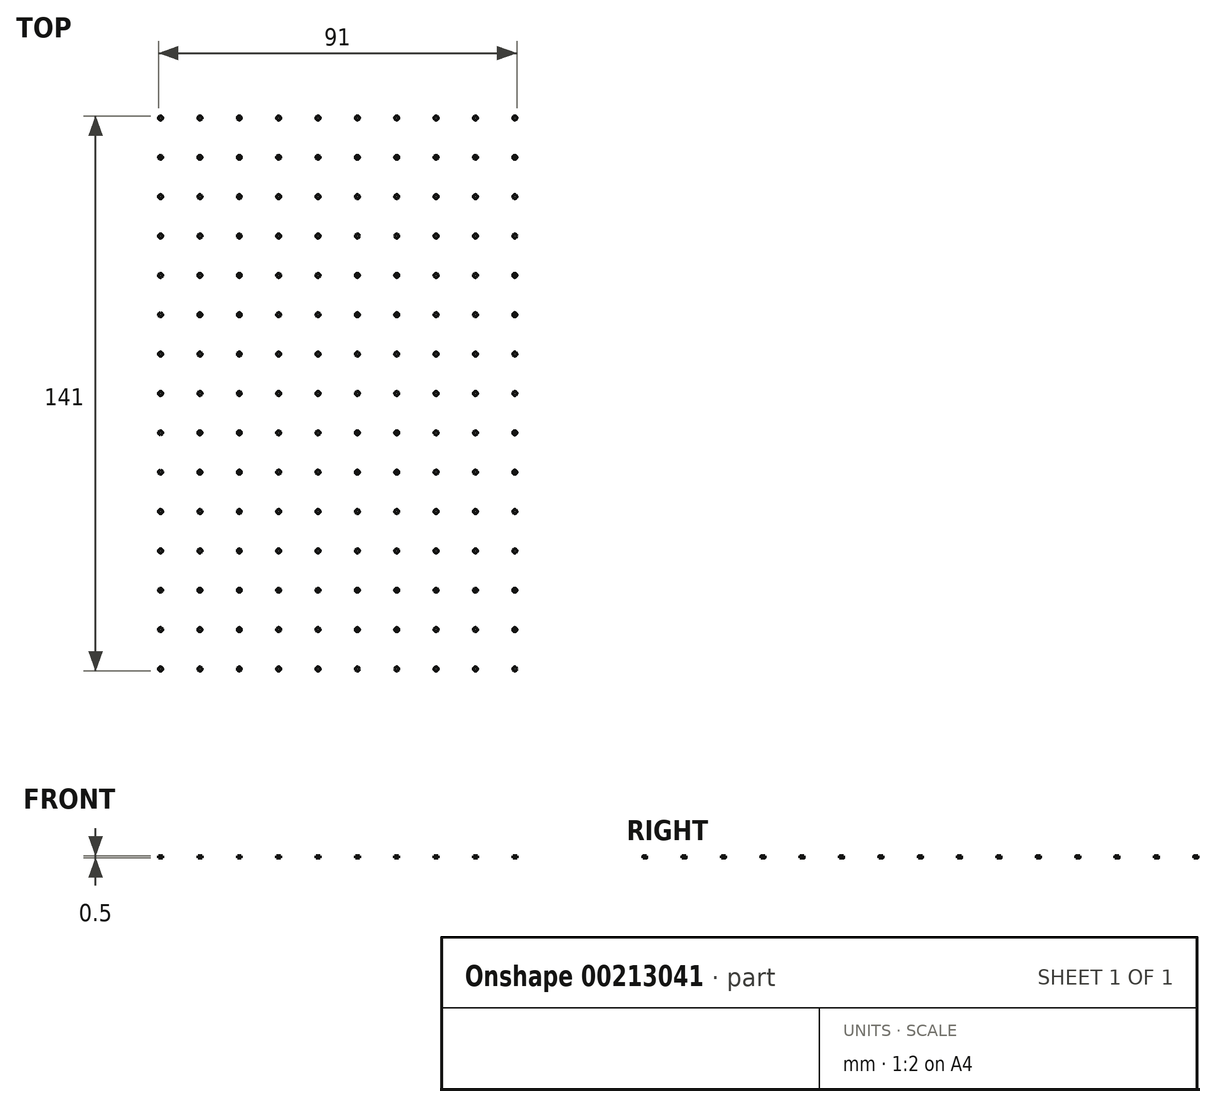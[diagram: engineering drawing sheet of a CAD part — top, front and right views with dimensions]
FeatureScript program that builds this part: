
annotation { "Feature Type Name" : "Feature", "Feature Type Description" : "" }
export const myFeature = defineFeature(function(context is Context, id is Id, definition is map)
    precondition{}
    {
        {
            var Q0;
            Q0=qCreatedBy(makeId("Top.planeOp"),FACE);
            var sketch = newSketch(context, id + "F0", { "sketchPlane" : qUnion([Q0])});
            skCircle(sketch, "E0", {"center": v(-61.45, -31.33) * mm, "radius": 0.5 * mm});
            skCircle(sketch, "E1.0.1.0", {"center": v(-61.45, -21.33) * mm, "radius": 0.5 * mm});
            skCircle(sketch, "E1.0.2.0", {"center": v(-61.45, -11.33) * mm, "radius": 0.5 * mm});
            skCircle(sketch, "E1.1.0.0", {"center": v(-51.45, -31.33) * mm, "radius": 0.5 * mm});
            skCircle(sketch, "E1.1.1.0", {"center": v(-51.45, -21.33) * mm, "radius": 0.5 * mm});
            skCircle(sketch, "E1.1.2.0", {"center": v(-51.45, -11.33) * mm, "radius": 0.5 * mm});
            skCircle(sketch, "E1.2.0.0", {"center": v(-41.45, -31.33) * mm, "radius": 0.5 * mm});
            skCircle(sketch, "E1.2.1.0", {"center": v(-41.45, -21.33) * mm, "radius": 0.5 * mm});
            skCircle(sketch, "E1.2.2.0", {"center": v(-41.45, -11.33) * mm, "radius": 0.5 * mm});
            skCircle(sketch, "E1.3.0.0", {"center": v(-31.45, -31.33) * mm, "radius": 0.5 * mm});
            skCircle(sketch, "E1.3.1.0", {"center": v(-31.45, -21.33) * mm, "radius": 0.5 * mm});
            skCircle(sketch, "E1.3.2.0", {"center": v(-31.45, -11.33) * mm, "radius": 0.5 * mm});
            skLineSegment(sketch, "E1.direction1", {"start": v(-61.45, -31.33) * mm, "end": v(-51.45, -31.33) * mm, "construction": true});
            skLineSegment(sketch, "E1.direction2", {"start": v(-61.45, -31.33) * mm, "end": v(-61.45, -21.33) * mm, "construction": true});
            skCircle(sketch, "E2.0.0.3", {"center": v(-61.45, -1.33) * mm, "radius": 0.5 * mm});
            skCircle(sketch, "E2.0.0.4", {"center": v(-61.45, 8.67) * mm, "radius": 0.5 * mm});
            skCircle(sketch, "E2.0.0.5", {"center": v(-61.45, 18.67) * mm, "radius": 0.5 * mm});
            skCircle(sketch, "E2.0.0.6", {"center": v(-61.45, 28.67) * mm, "radius": 0.5 * mm});
            skCircle(sketch, "E2.0.0.7", {"center": v(-61.45, 38.67) * mm, "radius": 0.5 * mm});
            skCircle(sketch, "E2.0.0.8", {"center": v(-61.45, 48.67) * mm, "radius": 0.5 * mm});
            skCircle(sketch, "E2.0.0.9", {"center": v(-61.45, 58.67) * mm, "radius": 0.5 * mm});
            skCircle(sketch, "E2.0.0.10", {"center": v(-61.45, 68.67) * mm, "radius": 0.5 * mm});
            skCircle(sketch, "E2.0.0.11", {"center": v(-61.45, 78.67) * mm, "radius": 0.5 * mm});
            skCircle(sketch, "E2.0.0.12", {"center": v(-61.45, 88.67) * mm, "radius": 0.5 * mm});
            skCircle(sketch, "E2.0.0.13", {"center": v(-61.45, 98.67) * mm, "radius": 0.5 * mm});
            skCircle(sketch, "E2.0.0.14", {"center": v(-61.45, 108.67) * mm, "radius": 0.5 * mm});
            skCircle(sketch, "E2.0.1.3", {"center": v(-51.45, -1.33) * mm, "radius": 0.5 * mm});
            skCircle(sketch, "E2.0.1.4", {"center": v(-51.45, 8.67) * mm, "radius": 0.5 * mm});
            skCircle(sketch, "E2.0.1.5", {"center": v(-51.45, 18.67) * mm, "radius": 0.5 * mm});
            skCircle(sketch, "E2.0.1.6", {"center": v(-51.45, 28.67) * mm, "radius": 0.5 * mm});
            skCircle(sketch, "E2.0.1.7", {"center": v(-51.45, 38.67) * mm, "radius": 0.5 * mm});
            skCircle(sketch, "E2.0.1.8", {"center": v(-51.45, 48.67) * mm, "radius": 0.5 * mm});
            skCircle(sketch, "E2.0.1.9", {"center": v(-51.45, 58.67) * mm, "radius": 0.5 * mm});
            skCircle(sketch, "E2.0.1.10", {"center": v(-51.45, 68.67) * mm, "radius": 0.5 * mm});
            skCircle(sketch, "E2.0.1.11", {"center": v(-51.45, 78.67) * mm, "radius": 0.5 * mm});
            skCircle(sketch, "E2.0.1.12", {"center": v(-51.45, 88.67) * mm, "radius": 0.5 * mm});
            skCircle(sketch, "E2.0.1.13", {"center": v(-51.45, 98.67) * mm, "radius": 0.5 * mm});
            skCircle(sketch, "E2.0.1.14", {"center": v(-51.45, 108.67) * mm, "radius": 0.5 * mm});
            skCircle(sketch, "E2.0.2.3", {"center": v(-41.45, -1.33) * mm, "radius": 0.5 * mm});
            skCircle(sketch, "E2.0.2.4", {"center": v(-41.45, 8.67) * mm, "radius": 0.5 * mm});
            skCircle(sketch, "E2.0.2.5", {"center": v(-41.45, 18.67) * mm, "radius": 0.5 * mm});
            skCircle(sketch, "E2.0.2.6", {"center": v(-41.45, 28.67) * mm, "radius": 0.5 * mm});
            skCircle(sketch, "E2.0.2.7", {"center": v(-41.45, 38.67) * mm, "radius": 0.5 * mm});
            skCircle(sketch, "E2.0.2.8", {"center": v(-41.45, 48.67) * mm, "radius": 0.5 * mm});
            skCircle(sketch, "E2.0.2.9", {"center": v(-41.45, 58.67) * mm, "radius": 0.5 * mm});
            skCircle(sketch, "E2.0.2.10", {"center": v(-41.45, 68.67) * mm, "radius": 0.5 * mm});
            skCircle(sketch, "E2.0.2.11", {"center": v(-41.45, 78.67) * mm, "radius": 0.5 * mm});
            skCircle(sketch, "E2.0.2.12", {"center": v(-41.45, 88.67) * mm, "radius": 0.5 * mm});
            skCircle(sketch, "E2.0.2.13", {"center": v(-41.45, 98.67) * mm, "radius": 0.5 * mm});
            skCircle(sketch, "E2.0.2.14", {"center": v(-41.45, 108.67) * mm, "radius": 0.5 * mm});
            skCircle(sketch, "E2.0.3.3", {"center": v(-31.45, -1.33) * mm, "radius": 0.5 * mm});
            skCircle(sketch, "E2.0.3.4", {"center": v(-31.45, 8.67) * mm, "radius": 0.5 * mm});
            skCircle(sketch, "E2.0.3.5", {"center": v(-31.45, 18.67) * mm, "radius": 0.5 * mm});
            skCircle(sketch, "E2.0.3.6", {"center": v(-31.45, 28.67) * mm, "radius": 0.5 * mm});
            skCircle(sketch, "E2.0.3.7", {"center": v(-31.45, 38.67) * mm, "radius": 0.5 * mm});
            skCircle(sketch, "E2.0.3.8", {"center": v(-31.45, 48.67) * mm, "radius": 0.5 * mm});
            skCircle(sketch, "E2.0.3.9", {"center": v(-31.45, 58.67) * mm, "radius": 0.5 * mm});
            skCircle(sketch, "E2.0.3.10", {"center": v(-31.45, 68.67) * mm, "radius": 0.5 * mm});
            skCircle(sketch, "E2.0.3.11", {"center": v(-31.45, 78.67) * mm, "radius": 0.5 * mm});
            skCircle(sketch, "E2.0.3.12", {"center": v(-31.45, 88.67) * mm, "radius": 0.5 * mm});
            skCircle(sketch, "E2.0.3.13", {"center": v(-31.45, 98.67) * mm, "radius": 0.5 * mm});
            skCircle(sketch, "E2.0.3.14", {"center": v(-31.45, 108.67) * mm, "radius": 0.5 * mm});
            skCircle(sketch, "E3.0.4.0", {"center": v(-21.45, -31.33) * mm, "radius": 0.5 * mm});
            skCircle(sketch, "E3.0.4.1", {"center": v(-21.45, -21.33) * mm, "radius": 0.5 * mm});
            skCircle(sketch, "E3.0.4.2", {"center": v(-21.45, -11.33) * mm, "radius": 0.5 * mm});
            skCircle(sketch, "E3.0.4.3", {"center": v(-21.45, -1.33) * mm, "radius": 0.5 * mm});
            skCircle(sketch, "E3.0.4.4", {"center": v(-21.45, 8.67) * mm, "radius": 0.5 * mm});
            skCircle(sketch, "E3.0.4.5", {"center": v(-21.45, 18.67) * mm, "radius": 0.5 * mm});
            skCircle(sketch, "E3.0.4.6", {"center": v(-21.45, 28.67) * mm, "radius": 0.5 * mm});
            skCircle(sketch, "E3.0.4.7", {"center": v(-21.45, 38.67) * mm, "radius": 0.5 * mm});
            skCircle(sketch, "E3.0.4.8", {"center": v(-21.45, 48.67) * mm, "radius": 0.5 * mm});
            skCircle(sketch, "E3.0.4.9", {"center": v(-21.45, 58.67) * mm, "radius": 0.5 * mm});
            skCircle(sketch, "E3.0.4.10", {"center": v(-21.45, 68.67) * mm, "radius": 0.5 * mm});
            skCircle(sketch, "E3.0.4.11", {"center": v(-21.45, 78.67) * mm, "radius": 0.5 * mm});
            skCircle(sketch, "E3.0.4.12", {"center": v(-21.45, 88.67) * mm, "radius": 0.5 * mm});
            skCircle(sketch, "E3.0.4.13", {"center": v(-21.45, 98.67) * mm, "radius": 0.5 * mm});
            skCircle(sketch, "E3.0.4.14", {"center": v(-21.45, 108.67) * mm, "radius": 0.5 * mm});
            skCircle(sketch, "E3.0.5.0", {"center": v(-11.45, -31.33) * mm, "radius": 0.5 * mm});
            skCircle(sketch, "E3.0.5.1", {"center": v(-11.45, -21.33) * mm, "radius": 0.5 * mm});
            skCircle(sketch, "E3.0.5.2", {"center": v(-11.45, -11.33) * mm, "radius": 0.5 * mm});
            skCircle(sketch, "E3.0.5.3", {"center": v(-11.45, -1.33) * mm, "radius": 0.5 * mm});
            skCircle(sketch, "E3.0.5.4", {"center": v(-11.45, 8.67) * mm, "radius": 0.5 * mm});
            skCircle(sketch, "E3.0.5.5", {"center": v(-11.45, 18.67) * mm, "radius": 0.5 * mm});
            skCircle(sketch, "E3.0.5.6", {"center": v(-11.45, 28.67) * mm, "radius": 0.5 * mm});
            skCircle(sketch, "E3.0.5.7", {"center": v(-11.45, 38.67) * mm, "radius": 0.5 * mm});
            skCircle(sketch, "E3.0.5.8", {"center": v(-11.45, 48.67) * mm, "radius": 0.5 * mm});
            skCircle(sketch, "E3.0.5.9", {"center": v(-11.45, 58.67) * mm, "radius": 0.5 * mm});
            skCircle(sketch, "E3.0.5.10", {"center": v(-11.45, 68.67) * mm, "radius": 0.5 * mm});
            skCircle(sketch, "E3.0.5.11", {"center": v(-11.45, 78.67) * mm, "radius": 0.5 * mm});
            skCircle(sketch, "E3.0.5.12", {"center": v(-11.45, 88.67) * mm, "radius": 0.5 * mm});
            skCircle(sketch, "E3.0.5.13", {"center": v(-11.45, 98.67) * mm, "radius": 0.5 * mm});
            skCircle(sketch, "E3.0.5.14", {"center": v(-11.45, 108.67) * mm, "radius": 0.5 * mm});
            skCircle(sketch, "E3.0.6.0", {"center": v(-1.45, -31.33) * mm, "radius": 0.5 * mm});
            skCircle(sketch, "E3.0.6.1", {"center": v(-1.45, -21.33) * mm, "radius": 0.5 * mm});
            skCircle(sketch, "E3.0.6.2", {"center": v(-1.45, -11.33) * mm, "radius": 0.5 * mm});
            skCircle(sketch, "E3.0.6.3", {"center": v(-1.45, -1.33) * mm, "radius": 0.5 * mm});
            skCircle(sketch, "E3.0.6.4", {"center": v(-1.45, 8.67) * mm, "radius": 0.5 * mm});
            skCircle(sketch, "E3.0.6.5", {"center": v(-1.45, 18.67) * mm, "radius": 0.5 * mm});
            skCircle(sketch, "E3.0.6.6", {"center": v(-1.45, 28.67) * mm, "radius": 0.5 * mm});
            skCircle(sketch, "E3.0.6.7", {"center": v(-1.45, 38.67) * mm, "radius": 0.5 * mm});
            skCircle(sketch, "E3.0.6.8", {"center": v(-1.45, 48.67) * mm, "radius": 0.5 * mm});
            skCircle(sketch, "E3.0.6.9", {"center": v(-1.45, 58.67) * mm, "radius": 0.5 * mm});
            skCircle(sketch, "E3.0.6.10", {"center": v(-1.45, 68.67) * mm, "radius": 0.5 * mm});
            skCircle(sketch, "E3.0.6.11", {"center": v(-1.45, 78.67) * mm, "radius": 0.5 * mm});
            skCircle(sketch, "E3.0.6.12", {"center": v(-1.45, 88.67) * mm, "radius": 0.5 * mm});
            skCircle(sketch, "E3.0.6.13", {"center": v(-1.45, 98.67) * mm, "radius": 0.5 * mm});
            skCircle(sketch, "E3.0.6.14", {"center": v(-1.45, 108.67) * mm, "radius": 0.5 * mm});
            skCircle(sketch, "E3.0.7.0", {"center": v(8.55, -31.33) * mm, "radius": 0.5 * mm});
            skCircle(sketch, "E3.0.7.1", {"center": v(8.55, -21.33) * mm, "radius": 0.5 * mm});
            skCircle(sketch, "E3.0.7.2", {"center": v(8.55, -11.33) * mm, "radius": 0.5 * mm});
            skCircle(sketch, "E3.0.7.3", {"center": v(8.55, -1.33) * mm, "radius": 0.5 * mm});
            skCircle(sketch, "E3.0.7.4", {"center": v(8.55, 8.67) * mm, "radius": 0.5 * mm});
            skCircle(sketch, "E3.0.7.5", {"center": v(8.55, 18.67) * mm, "radius": 0.5 * mm});
            skCircle(sketch, "E3.0.7.6", {"center": v(8.55, 28.67) * mm, "radius": 0.5 * mm});
            skCircle(sketch, "E3.0.7.7", {"center": v(8.55, 38.67) * mm, "radius": 0.5 * mm});
            skCircle(sketch, "E3.0.7.8", {"center": v(8.55, 48.67) * mm, "radius": 0.5 * mm});
            skCircle(sketch, "E3.0.7.9", {"center": v(8.55, 58.67) * mm, "radius": 0.5 * mm});
            skCircle(sketch, "E3.0.7.10", {"center": v(8.55, 68.67) * mm, "radius": 0.5 * mm});
            skCircle(sketch, "E3.0.7.11", {"center": v(8.55, 78.67) * mm, "radius": 0.5 * mm});
            skCircle(sketch, "E3.0.7.12", {"center": v(8.55, 88.67) * mm, "radius": 0.5 * mm});
            skCircle(sketch, "E3.0.7.13", {"center": v(8.55, 98.67) * mm, "radius": 0.5 * mm});
            skCircle(sketch, "E3.0.7.14", {"center": v(8.55, 108.67) * mm, "radius": 0.5 * mm});
            skCircle(sketch, "E3.0.8.0", {"center": v(18.55, -31.33) * mm, "radius": 0.5 * mm});
            skCircle(sketch, "E3.0.8.1", {"center": v(18.55, -21.33) * mm, "radius": 0.5 * mm});
            skCircle(sketch, "E3.0.8.2", {"center": v(18.55, -11.33) * mm, "radius": 0.5 * mm});
            skCircle(sketch, "E3.0.8.3", {"center": v(18.55, -1.33) * mm, "radius": 0.5 * mm});
            skCircle(sketch, "E3.0.8.4", {"center": v(18.55, 8.67) * mm, "radius": 0.5 * mm});
            skCircle(sketch, "E3.0.8.5", {"center": v(18.55, 18.67) * mm, "radius": 0.5 * mm});
            skCircle(sketch, "E3.0.8.6", {"center": v(18.55, 28.67) * mm, "radius": 0.5 * mm});
            skCircle(sketch, "E3.0.8.7", {"center": v(18.55, 38.67) * mm, "radius": 0.5 * mm});
            skCircle(sketch, "E3.0.8.8", {"center": v(18.55, 48.67) * mm, "radius": 0.5 * mm});
            skCircle(sketch, "E3.0.8.9", {"center": v(18.55, 58.67) * mm, "radius": 0.5 * mm});
            skCircle(sketch, "E3.0.8.10", {"center": v(18.55, 68.67) * mm, "radius": 0.5 * mm});
            skCircle(sketch, "E3.0.8.11", {"center": v(18.55, 78.67) * mm, "radius": 0.5 * mm});
            skCircle(sketch, "E3.0.8.12", {"center": v(18.55, 88.67) * mm, "radius": 0.5 * mm});
            skCircle(sketch, "E3.0.8.13", {"center": v(18.55, 98.67) * mm, "radius": 0.5 * mm});
            skCircle(sketch, "E3.0.8.14", {"center": v(18.55, 108.67) * mm, "radius": 0.5 * mm});
            skCircle(sketch, "E3.0.9.0", {"center": v(28.55, -31.33) * mm, "radius": 0.5 * mm});
            skCircle(sketch, "E3.0.9.1", {"center": v(28.55, -21.33) * mm, "radius": 0.5 * mm});
            skCircle(sketch, "E3.0.9.2", {"center": v(28.55, -11.33) * mm, "radius": 0.5 * mm});
            skCircle(sketch, "E3.0.9.3", {"center": v(28.55, -1.33) * mm, "radius": 0.5 * mm});
            skCircle(sketch, "E3.0.9.4", {"center": v(28.55, 8.67) * mm, "radius": 0.5 * mm});
            skCircle(sketch, "E3.0.9.5", {"center": v(28.55, 18.67) * mm, "radius": 0.5 * mm});
            skCircle(sketch, "E3.0.9.6", {"center": v(28.55, 28.67) * mm, "radius": 0.5 * mm});
            skCircle(sketch, "E3.0.9.7", {"center": v(28.55, 38.67) * mm, "radius": 0.5 * mm});
            skCircle(sketch, "E3.0.9.8", {"center": v(28.55, 48.67) * mm, "radius": 0.5 * mm});
            skCircle(sketch, "E3.0.9.9", {"center": v(28.55, 58.67) * mm, "radius": 0.5 * mm});
            skCircle(sketch, "E3.0.9.10", {"center": v(28.55, 68.67) * mm, "radius": 0.5 * mm});
            skCircle(sketch, "E3.0.9.11", {"center": v(28.55, 78.67) * mm, "radius": 0.5 * mm});
            skCircle(sketch, "E3.0.9.12", {"center": v(28.55, 88.67) * mm, "radius": 0.5 * mm});
            skCircle(sketch, "E3.0.9.13", {"center": v(28.55, 98.67) * mm, "radius": 0.5 * mm});
            skCircle(sketch, "E3.0.9.14", {"center": v(28.55, 108.67) * mm, "radius": 0.5 * mm});
            skSolve(sketch);
        }
        {
            var Q0;
            Q0=makeQuery(id+"F0.imprint","IMPRINT",FACE,{"disambiguationData":[TD([[makeQuery(id+"F0.imprint","IMPRINT",EDGE,{"derivedFrom":sQuery(id+"F0.wireOp",EDGE,"E1.0.2.0")}),1.0]])]});
            var Q1;
            Q1=makeQuery(id+"F0.imprint","IMPRINT",FACE,{"disambiguationData":[TD([[makeQuery(id+"F0.imprint","IMPRINT",EDGE,{"derivedFrom":sQuery(id+"F0.wireOp",EDGE,"E1.3.2.0")}),1.0]])]});
            var Q2;
            Q2=makeQuery(id+"F0.imprint","IMPRINT",FACE,{"disambiguationData":[TD([[makeQuery(id+"F0.imprint","IMPRINT",EDGE,{"derivedFrom":sQuery(id+"F0.wireOp",EDGE,"E1.3.1.0")}),1.0]])]});
            var Q3;
            Q3=makeQuery(id+"F0.imprint","IMPRINT",FACE,{"disambiguationData":[TD([[makeQuery(id+"F0.imprint","IMPRINT",EDGE,{"derivedFrom":sQuery(id+"F0.wireOp",EDGE,"E1.3.0.0")}),1.0]])]});
            var Q4;
            Q4=makeQuery(id+"F0.imprint","IMPRINT",FACE,{"disambiguationData":[TD([[makeQuery(id+"F0.imprint","IMPRINT",EDGE,{"derivedFrom":sQuery(id+"F0.wireOp",EDGE,"E1.2.2.0")}),1.0]])]});
            var Q5;
            Q5=makeQuery(id+"F0.imprint","IMPRINT",FACE,{"disambiguationData":[TD([[makeQuery(id+"F0.imprint","IMPRINT",EDGE,{"derivedFrom":sQuery(id+"F0.wireOp",EDGE,"E1.2.1.0")}),1.0]])]});
            var Q6;
            Q6=makeQuery(id+"F0.imprint","IMPRINT",FACE,{"disambiguationData":[TD([[makeQuery(id+"F0.imprint","IMPRINT",EDGE,{"derivedFrom":sQuery(id+"F0.wireOp",EDGE,"E1.2.0.0")}),1.0]])]});
            var Q7;
            Q7=makeQuery(id+"F0.imprint","IMPRINT",FACE,{"disambiguationData":[TD([[makeQuery(id+"F0.imprint","IMPRINT",EDGE,{"derivedFrom":sQuery(id+"F0.wireOp",EDGE,"E1.1.2.0")}),1.0]])]});
            var Q8;
            Q8=makeQuery(id+"F0.imprint","IMPRINT",FACE,{"disambiguationData":[TD([[makeQuery(id+"F0.imprint","IMPRINT",EDGE,{"derivedFrom":sQuery(id+"F0.wireOp",EDGE,"E1.1.1.0")}),1.0]])]});
            var Q9;
            Q9=makeQuery(id+"F0.imprint","IMPRINT",FACE,{"disambiguationData":[TD([[makeQuery(id+"F0.imprint","IMPRINT",EDGE,{"derivedFrom":sQuery(id+"F0.wireOp",EDGE,"E1.1.0.0")}),1.0]])]});
            var Q10;
            Q10=makeQuery(id+"F0.imprint","IMPRINT",FACE,{"disambiguationData":[TD([[makeQuery(id+"F0.imprint","IMPRINT",EDGE,{"derivedFrom":sQuery(id+"F0.wireOp",EDGE,"E1.0.1.0")}),1.0]])]});
            var Q11;
            Q11=makeQuery(id+"F0.imprint","IMPRINT",FACE,{"disambiguationData":[TD([[makeQuery(id+"F0.imprint","IMPRINT",EDGE,{"derivedFrom":sQuery(id+"F0.wireOp",EDGE,"E0")}),1.0]])]});
            var Q12;
            Q12=makeQuery(id+"F0.imprint","IMPRINT",FACE,{"disambiguationData":[TD([[makeQuery(id+"F0.imprint","IMPRINT",EDGE,{"derivedFrom":sQuery(id+"F0.wireOp",EDGE,"E2.0.2.13")}),1.0]])]});
            var Q13;
            Q13=makeQuery(id+"F0.imprint","IMPRINT",FACE,{"disambiguationData":[TD([[makeQuery(id+"F0.imprint","IMPRINT",EDGE,{"derivedFrom":sQuery(id+"F0.wireOp",EDGE,"E3.0.9.5")}),1.0]])]});
            var Q14;
            Q14=makeQuery(id+"F0.imprint","IMPRINT",FACE,{"disambiguationData":[TD([[makeQuery(id+"F0.imprint","IMPRINT",EDGE,{"derivedFrom":sQuery(id+"F0.wireOp",EDGE,"E3.0.5.1")}),1.0]])]});
            var Q15;
            Q15=makeQuery(id+"F0.imprint","IMPRINT",FACE,{"disambiguationData":[TD([[makeQuery(id+"F0.imprint","IMPRINT",EDGE,{"derivedFrom":sQuery(id+"F0.wireOp",EDGE,"E2.0.1.7")}),1.0]])]});
            var Q16;
            Q16=makeQuery(id+"F0.imprint","IMPRINT",FACE,{"disambiguationData":[TD([[makeQuery(id+"F0.imprint","IMPRINT",EDGE,{"derivedFrom":sQuery(id+"F0.wireOp",EDGE,"E2.0.2.11")}),1.0]])]});
            var Q17;
            Q17=makeQuery(id+"F0.imprint","IMPRINT",FACE,{"disambiguationData":[TD([[makeQuery(id+"F0.imprint","IMPRINT",EDGE,{"derivedFrom":sQuery(id+"F0.wireOp",EDGE,"E3.0.4.0")}),1.0]])]});
            var Q18;
            Q18=makeQuery(id+"F0.imprint","IMPRINT",FACE,{"disambiguationData":[TD([[makeQuery(id+"F0.imprint","IMPRINT",EDGE,{"derivedFrom":sQuery(id+"F0.wireOp",EDGE,"E3.0.7.5")}),1.0]])]});
            var Q19;
            Q19=makeQuery(id+"F0.imprint","IMPRINT",FACE,{"disambiguationData":[TD([[makeQuery(id+"F0.imprint","IMPRINT",EDGE,{"derivedFrom":sQuery(id+"F0.wireOp",EDGE,"E3.0.8.6")}),1.0]])]});
            var Q20;
            Q20=makeQuery(id+"F0.imprint","IMPRINT",FACE,{"disambiguationData":[TD([[makeQuery(id+"F0.imprint","IMPRINT",EDGE,{"derivedFrom":sQuery(id+"F0.wireOp",EDGE,"E3.0.5.0")}),1.0]])]});
            var Q21;
            Q21=makeQuery(id+"F0.imprint","IMPRINT",FACE,{"disambiguationData":[TD([[makeQuery(id+"F0.imprint","IMPRINT",EDGE,{"derivedFrom":sQuery(id+"F0.wireOp",EDGE,"E3.0.7.2")}),1.0]])]});
            var Q22;
            Q22=makeQuery(id+"F0.imprint","IMPRINT",FACE,{"disambiguationData":[TD([[makeQuery(id+"F0.imprint","IMPRINT",EDGE,{"derivedFrom":sQuery(id+"F0.wireOp",EDGE,"E3.0.6.1")}),1.0]])]});
            var Q23;
            Q23=makeQuery(id+"F0.imprint","IMPRINT",FACE,{"disambiguationData":[TD([[makeQuery(id+"F0.imprint","IMPRINT",EDGE,{"derivedFrom":sQuery(id+"F0.wireOp",EDGE,"E3.0.6.7")}),1.0]])]});
            var Q24;
            Q24=makeQuery(id+"F0.imprint","IMPRINT",FACE,{"disambiguationData":[TD([[makeQuery(id+"F0.imprint","IMPRINT",EDGE,{"derivedFrom":sQuery(id+"F0.wireOp",EDGE,"E3.0.6.2")}),1.0]])]});
            var Q25;
            Q25=makeQuery(id+"F0.imprint","IMPRINT",FACE,{"disambiguationData":[TD([[makeQuery(id+"F0.imprint","IMPRINT",EDGE,{"derivedFrom":sQuery(id+"F0.wireOp",EDGE,"E3.0.9.4")}),1.0]])]});
            var Q26;
            Q26=makeQuery(id+"F0.imprint","IMPRINT",FACE,{"disambiguationData":[TD([[makeQuery(id+"F0.imprint","IMPRINT",EDGE,{"derivedFrom":sQuery(id+"F0.wireOp",EDGE,"E3.0.4.2")}),1.0]])]});
            var Q27;
            Q27=makeQuery(id+"F0.imprint","IMPRINT",FACE,{"disambiguationData":[TD([[makeQuery(id+"F0.imprint","IMPRINT",EDGE,{"derivedFrom":sQuery(id+"F0.wireOp",EDGE,"E3.0.5.7")}),1.0]])]});
            var Q28;
            Q28=makeQuery(id+"F0.imprint","IMPRINT",FACE,{"disambiguationData":[TD([[makeQuery(id+"F0.imprint","IMPRINT",EDGE,{"derivedFrom":sQuery(id+"F0.wireOp",EDGE,"E3.0.8.4")}),1.0]])]});
            var Q29;
            Q29=makeQuery(id+"F0.imprint","IMPRINT",FACE,{"disambiguationData":[TD([[makeQuery(id+"F0.imprint","IMPRINT",EDGE,{"derivedFrom":sQuery(id+"F0.wireOp",EDGE,"E3.0.9.7")}),1.0]])]});
            var Q30;
            Q30=makeQuery(id+"F0.imprint","IMPRINT",FACE,{"disambiguationData":[TD([[makeQuery(id+"F0.imprint","IMPRINT",EDGE,{"derivedFrom":sQuery(id+"F0.wireOp",EDGE,"E2.0.1.9")}),1.0]])]});
            var Q31;
            Q31=makeQuery(id+"F0.imprint","IMPRINT",FACE,{"disambiguationData":[TD([[makeQuery(id+"F0.imprint","IMPRINT",EDGE,{"derivedFrom":sQuery(id+"F0.wireOp",EDGE,"E3.0.5.3")}),1.0]])]});
            var Q32;
            Q32=makeQuery(id+"F0.imprint","IMPRINT",FACE,{"disambiguationData":[TD([[makeQuery(id+"F0.imprint","IMPRINT",EDGE,{"derivedFrom":sQuery(id+"F0.wireOp",EDGE,"E3.0.6.8")}),1.0]])]});
            var Q33;
            Q33=makeQuery(id+"F0.imprint","IMPRINT",FACE,{"disambiguationData":[TD([[makeQuery(id+"F0.imprint","IMPRINT",EDGE,{"derivedFrom":sQuery(id+"F0.wireOp",EDGE,"E3.0.6.4")}),1.0]])]});
            var Q34;
            Q34=makeQuery(id+"F0.imprint","IMPRINT",FACE,{"disambiguationData":[TD([[makeQuery(id+"F0.imprint","IMPRINT",EDGE,{"derivedFrom":sQuery(id+"F0.wireOp",EDGE,"E3.0.7.3")}),1.0]])]});
            var Q35;
            Q35=makeQuery(id+"F0.imprint","IMPRINT",FACE,{"disambiguationData":[TD([[makeQuery(id+"F0.imprint","IMPRINT",EDGE,{"derivedFrom":sQuery(id+"F0.wireOp",EDGE,"E2.0.3.3")}),1.0]])]});
            var Q36;
            Q36=makeQuery(id+"F0.imprint","IMPRINT",FACE,{"disambiguationData":[TD([[makeQuery(id+"F0.imprint","IMPRINT",EDGE,{"derivedFrom":sQuery(id+"F0.wireOp",EDGE,"E3.0.9.11")}),1.0]])]});
            var Q37;
            Q37=makeQuery(id+"F0.imprint","IMPRINT",FACE,{"disambiguationData":[TD([[makeQuery(id+"F0.imprint","IMPRINT",EDGE,{"derivedFrom":sQuery(id+"F0.wireOp",EDGE,"E3.0.4.6")}),1.0]])]});
            var Q38;
            Q38=makeQuery(id+"F0.imprint","IMPRINT",FACE,{"disambiguationData":[TD([[makeQuery(id+"F0.imprint","IMPRINT",EDGE,{"derivedFrom":sQuery(id+"F0.wireOp",EDGE,"E3.0.6.5")}),1.0]])]});
            var Q39;
            Q39=makeQuery(id+"F0.imprint","IMPRINT",FACE,{"disambiguationData":[TD([[makeQuery(id+"F0.imprint","IMPRINT",EDGE,{"derivedFrom":sQuery(id+"F0.wireOp",EDGE,"E3.0.4.12")}),1.0]])]});
            var Q40;
            Q40=makeQuery(id+"F0.imprint","IMPRINT",FACE,{"disambiguationData":[TD([[makeQuery(id+"F0.imprint","IMPRINT",EDGE,{"derivedFrom":sQuery(id+"F0.wireOp",EDGE,"E2.0.1.11")}),1.0]])]});
            var Q41;
            Q41=makeQuery(id+"F0.imprint","IMPRINT",FACE,{"disambiguationData":[TD([[makeQuery(id+"F0.imprint","IMPRINT",EDGE,{"derivedFrom":sQuery(id+"F0.wireOp",EDGE,"E3.0.4.4")}),1.0]])]});
            var Q42;
            Q42=makeQuery(id+"F0.imprint","IMPRINT",FACE,{"disambiguationData":[TD([[makeQuery(id+"F0.imprint","IMPRINT",EDGE,{"derivedFrom":sQuery(id+"F0.wireOp",EDGE,"E3.0.5.14")}),1.0]])]});
            var Q43;
            Q43=makeQuery(id+"F0.imprint","IMPRINT",FACE,{"disambiguationData":[TD([[makeQuery(id+"F0.imprint","IMPRINT",EDGE,{"derivedFrom":sQuery(id+"F0.wireOp",EDGE,"E3.0.4.3")}),1.0]])]});
            var Q44;
            Q44=makeQuery(id+"F0.imprint","IMPRINT",FACE,{"disambiguationData":[TD([[makeQuery(id+"F0.imprint","IMPRINT",EDGE,{"derivedFrom":sQuery(id+"F0.wireOp",EDGE,"E3.0.5.5")}),1.0]])]});
            var Q45;
            Q45=makeQuery(id+"F0.imprint","IMPRINT",FACE,{"disambiguationData":[TD([[makeQuery(id+"F0.imprint","IMPRINT",EDGE,{"derivedFrom":sQuery(id+"F0.wireOp",EDGE,"E3.0.7.9")}),1.0]])]});
            var Q46;
            Q46=makeQuery(id+"F0.imprint","IMPRINT",FACE,{"disambiguationData":[TD([[makeQuery(id+"F0.imprint","IMPRINT",EDGE,{"derivedFrom":sQuery(id+"F0.wireOp",EDGE,"E2.0.0.7")}),1.0]])]});
            var Q47;
            Q47=makeQuery(id+"F0.imprint","IMPRINT",FACE,{"disambiguationData":[TD([[makeQuery(id+"F0.imprint","IMPRINT",EDGE,{"derivedFrom":sQuery(id+"F0.wireOp",EDGE,"E2.0.1.13")}),1.0]])]});
            var Q48;
            Q48=makeQuery(id+"F0.imprint","IMPRINT",FACE,{"disambiguationData":[TD([[makeQuery(id+"F0.imprint","IMPRINT",EDGE,{"derivedFrom":sQuery(id+"F0.wireOp",EDGE,"E2.0.3.5")}),1.0]])]});
            var Q49;
            Q49=makeQuery(id+"F0.imprint","IMPRINT",FACE,{"disambiguationData":[TD([[makeQuery(id+"F0.imprint","IMPRINT",EDGE,{"derivedFrom":sQuery(id+"F0.wireOp",EDGE,"E3.0.7.0")}),1.0]])]});
            var Q50;
            Q50=makeQuery(id+"F0.imprint","IMPRINT",FACE,{"disambiguationData":[TD([[makeQuery(id+"F0.imprint","IMPRINT",EDGE,{"derivedFrom":sQuery(id+"F0.wireOp",EDGE,"E3.0.8.3")}),1.0]])]});
            var Q51;
            Q51=makeQuery(id+"F0.imprint","IMPRINT",FACE,{"disambiguationData":[TD([[makeQuery(id+"F0.imprint","IMPRINT",EDGE,{"derivedFrom":sQuery(id+"F0.wireOp",EDGE,"E2.0.1.6")}),1.0]])]});
            var Q52;
            Q52=makeQuery(id+"F0.imprint","IMPRINT",FACE,{"disambiguationData":[TD([[makeQuery(id+"F0.imprint","IMPRINT",EDGE,{"derivedFrom":sQuery(id+"F0.wireOp",EDGE,"E2.0.2.10")}),1.0]])]});
            var Q53;
            Q53=makeQuery(id+"F0.imprint","IMPRINT",FACE,{"disambiguationData":[TD([[makeQuery(id+"F0.imprint","IMPRINT",EDGE,{"derivedFrom":sQuery(id+"F0.wireOp",EDGE,"E2.0.3.14")}),1.0]])]});
            var Q54;
            Q54=makeQuery(id+"F0.imprint","IMPRINT",FACE,{"disambiguationData":[TD([[makeQuery(id+"F0.imprint","IMPRINT",EDGE,{"derivedFrom":sQuery(id+"F0.wireOp",EDGE,"E3.0.6.3")}),1.0]])]});
            var Q55;
            Q55=makeQuery(id+"F0.imprint","IMPRINT",FACE,{"disambiguationData":[TD([[makeQuery(id+"F0.imprint","IMPRINT",EDGE,{"derivedFrom":sQuery(id+"F0.wireOp",EDGE,"E3.0.7.4")}),1.0]])]});
            var Q56;
            Q56=makeQuery(id+"F0.imprint","IMPRINT",FACE,{"disambiguationData":[TD([[makeQuery(id+"F0.imprint","IMPRINT",EDGE,{"derivedFrom":sQuery(id+"F0.wireOp",EDGE,"E3.0.8.5")}),1.0]])]});
            var Q57;
            Q57=makeQuery(id+"F0.imprint","IMPRINT",FACE,{"disambiguationData":[TD([[makeQuery(id+"F0.imprint","IMPRINT",EDGE,{"derivedFrom":sQuery(id+"F0.wireOp",EDGE,"E3.0.9.6")}),1.0]])]});
            var Q58;
            Q58=makeQuery(id+"F0.imprint","IMPRINT",FACE,{"disambiguationData":[TD([[makeQuery(id+"F0.imprint","IMPRINT",EDGE,{"derivedFrom":sQuery(id+"F0.wireOp",EDGE,"E2.0.1.8")}),1.0]])]});
            var Q59;
            Q59=makeQuery(id+"F0.imprint","IMPRINT",FACE,{"disambiguationData":[TD([[makeQuery(id+"F0.imprint","IMPRINT",EDGE,{"derivedFrom":sQuery(id+"F0.wireOp",EDGE,"E2.0.2.12")}),1.0]])]});
            var Q60;
            Q60=makeQuery(id+"F0.imprint","IMPRINT",FACE,{"disambiguationData":[TD([[makeQuery(id+"F0.imprint","IMPRINT",EDGE,{"derivedFrom":sQuery(id+"F0.wireOp",EDGE,"E3.0.4.1")}),1.0]])]});
            var Q61;
            Q61=makeQuery(id+"F0.imprint","IMPRINT",FACE,{"disambiguationData":[TD([[makeQuery(id+"F0.imprint","IMPRINT",EDGE,{"derivedFrom":sQuery(id+"F0.wireOp",EDGE,"E3.0.7.8")}),1.0]])]});
            var Q62;
            Q62=makeQuery(id+"F0.imprint","IMPRINT",FACE,{"disambiguationData":[TD([[makeQuery(id+"F0.imprint","IMPRINT",EDGE,{"derivedFrom":sQuery(id+"F0.wireOp",EDGE,"E3.0.5.2")}),1.0]])]});
            var Q63;
            Q63=makeQuery(id+"F0.imprint","IMPRINT",FACE,{"disambiguationData":[TD([[makeQuery(id+"F0.imprint","IMPRINT",EDGE,{"derivedFrom":sQuery(id+"F0.wireOp",EDGE,"E3.0.8.9")}),1.0]])]});
            var Q64;
            Q64=makeQuery(id+"F0.imprint","IMPRINT",FACE,{"disambiguationData":[TD([[makeQuery(id+"F0.imprint","IMPRINT",EDGE,{"derivedFrom":sQuery(id+"F0.wireOp",EDGE,"E3.0.9.10")}),1.0]])]});
            var Q65;
            Q65=makeQuery(id+"F0.imprint","IMPRINT",FACE,{"disambiguationData":[TD([[makeQuery(id+"F0.imprint","IMPRINT",EDGE,{"derivedFrom":sQuery(id+"F0.wireOp",EDGE,"E3.0.9.3")}),1.0]])]});
            var Q66;
            Q66=makeQuery(id+"F0.imprint","IMPRINT",FACE,{"disambiguationData":[TD([[makeQuery(id+"F0.imprint","IMPRINT",EDGE,{"derivedFrom":sQuery(id+"F0.wireOp",EDGE,"E2.0.1.12")}),1.0]])]});
            var Q67;
            Q67=makeQuery(id+"F0.imprint","IMPRINT",FACE,{"disambiguationData":[TD([[makeQuery(id+"F0.imprint","IMPRINT",EDGE,{"derivedFrom":sQuery(id+"F0.wireOp",EDGE,"E2.0.3.4")}),1.0]])]});
            var Q68;
            Q68=makeQuery(id+"F0.imprint","IMPRINT",FACE,{"disambiguationData":[TD([[makeQuery(id+"F0.imprint","IMPRINT",EDGE,{"derivedFrom":sQuery(id+"F0.wireOp",EDGE,"E3.0.4.14")}),1.0]])]});
            var Q69;
            Q69=makeQuery(id+"F0.imprint","IMPRINT",FACE,{"disambiguationData":[TD([[makeQuery(id+"F0.imprint","IMPRINT",EDGE,{"derivedFrom":sQuery(id+"F0.wireOp",EDGE,"E3.0.4.5")}),1.0]])]});
            var Q70;
            Q70=makeQuery(id+"F0.imprint","IMPRINT",FACE,{"disambiguationData":[TD([[makeQuery(id+"F0.imprint","IMPRINT",EDGE,{"derivedFrom":sQuery(id+"F0.wireOp",EDGE,"E3.0.5.6")}),1.0]])]});
            var Q71;
            Q71=makeQuery(id+"F0.imprint","IMPRINT",FACE,{"disambiguationData":[TD([[makeQuery(id+"F0.imprint","IMPRINT",EDGE,{"derivedFrom":sQuery(id+"F0.wireOp",EDGE,"E2.0.0.8")}),1.0]])]});
            var Q72;
            Q72=makeQuery(id+"F0.imprint","IMPRINT",FACE,{"disambiguationData":[TD([[makeQuery(id+"F0.imprint","IMPRINT",EDGE,{"derivedFrom":sQuery(id+"F0.wireOp",EDGE,"E3.0.6.0")}),1.0]])]});
            var Q73;
            Q73=makeQuery(id+"F0.imprint","IMPRINT",FACE,{"disambiguationData":[TD([[makeQuery(id+"F0.imprint","IMPRINT",EDGE,{"derivedFrom":sQuery(id+"F0.wireOp",EDGE,"E3.0.7.1")}),1.0]])]});
            var Q74;
            Q74=makeQuery(id+"F0.imprint","IMPRINT",FACE,{"disambiguationData":[TD([[makeQuery(id+"F0.imprint","IMPRINT",EDGE,{"derivedFrom":sQuery(id+"F0.wireOp",EDGE,"E3.0.8.2")}),1.0]])]});
            var Q75;
            Q75=makeQuery(id+"F0.imprint","IMPRINT",FACE,{"disambiguationData":[TD([[makeQuery(id+"F0.imprint","IMPRINT",EDGE,{"derivedFrom":sQuery(id+"F0.wireOp",EDGE,"E2.0.1.5")}),1.0]])]});
            var Q76;
            Q76=makeQuery(id+"F0.imprint","IMPRINT",FACE,{"disambiguationData":[TD([[makeQuery(id+"F0.imprint","IMPRINT",EDGE,{"derivedFrom":sQuery(id+"F0.wireOp",EDGE,"E2.0.2.9")}),1.0]])]});
            var Q77;
            Q77=makeQuery(id+"F0.imprint","IMPRINT",FACE,{"disambiguationData":[TD([[makeQuery(id+"F0.imprint","IMPRINT",EDGE,{"derivedFrom":sQuery(id+"F0.wireOp",EDGE,"E3.0.6.6")}),1.0]])]});
            var Q78;
            Q78=makeQuery(id+"F0.imprint","IMPRINT",FACE,{"disambiguationData":[TD([[makeQuery(id+"F0.imprint","IMPRINT",EDGE,{"derivedFrom":sQuery(id+"F0.wireOp",EDGE,"E3.0.7.7")}),1.0]])]});
            var Q79;
            Q79=makeQuery(id+"F0.imprint","IMPRINT",FACE,{"disambiguationData":[TD([[makeQuery(id+"F0.imprint","IMPRINT",EDGE,{"derivedFrom":sQuery(id+"F0.wireOp",EDGE,"E2.0.3.13")}),1.0]])]});
            var Q80;
            Q80=makeQuery(id+"F0.imprint","IMPRINT",FACE,{"disambiguationData":[TD([[makeQuery(id+"F0.imprint","IMPRINT",EDGE,{"derivedFrom":sQuery(id+"F0.wireOp",EDGE,"E3.0.8.8")}),1.0]])]});
            var Q81;
            Q81=makeQuery(id+"F0.imprint","IMPRINT",FACE,{"disambiguationData":[TD([[makeQuery(id+"F0.imprint","IMPRINT",EDGE,{"derivedFrom":sQuery(id+"F0.wireOp",EDGE,"E3.0.9.9")}),1.0]])]});
            var Q82;
            Q82=makeQuery(id+"F0.imprint","IMPRINT",FACE,{"disambiguationData":[TD([[makeQuery(id+"F0.imprint","IMPRINT",EDGE,{"derivedFrom":sQuery(id+"F0.wireOp",EDGE,"E3.0.5.4")}),1.0]])]});
            var Q83;
            Q83=makeQuery(id+"F0.imprint","IMPRINT",FACE,{"disambiguationData":[TD([[makeQuery(id+"F0.imprint","IMPRINT",EDGE,{"derivedFrom":sQuery(id+"F0.wireOp",EDGE,"E3.0.7.6")}),1.0]])]});
            var Q84;
            Q84=makeQuery(id+"F0.imprint","IMPRINT",FACE,{"disambiguationData":[TD([[makeQuery(id+"F0.imprint","IMPRINT",EDGE,{"derivedFrom":sQuery(id+"F0.wireOp",EDGE,"E2.0.0.10")}),1.0]])]});
            var Q85;
            Q85=makeQuery(id+"F0.imprint","IMPRINT",FACE,{"disambiguationData":[TD([[makeQuery(id+"F0.imprint","IMPRINT",EDGE,{"derivedFrom":sQuery(id+"F0.wireOp",EDGE,"E3.0.5.8")}),1.0]])]});
            var Q86;
            Q86=makeQuery(id+"F0.imprint","IMPRINT",FACE,{"disambiguationData":[TD([[makeQuery(id+"F0.imprint","IMPRINT",EDGE,{"derivedFrom":sQuery(id+"F0.wireOp",EDGE,"E3.0.4.7")}),1.0]])]});
            var Q87;
            Q87=makeQuery(id+"F0.imprint","IMPRINT",FACE,{"disambiguationData":[TD([[makeQuery(id+"F0.imprint","IMPRINT",EDGE,{"derivedFrom":sQuery(id+"F0.wireOp",EDGE,"E2.0.3.6")}),1.0]])]});
            var Q88;
            Q88=makeQuery(id+"F0.imprint","IMPRINT",FACE,{"disambiguationData":[TD([[makeQuery(id+"F0.imprint","IMPRINT",EDGE,{"derivedFrom":sQuery(id+"F0.wireOp",EDGE,"E2.0.1.14")}),1.0]])]});
            var Q89;
            Q89=makeQuery(id+"F0.imprint","IMPRINT",FACE,{"disambiguationData":[TD([[makeQuery(id+"F0.imprint","IMPRINT",EDGE,{"derivedFrom":sQuery(id+"F0.wireOp",EDGE,"E3.0.9.12")}),1.0]])]});
            var Q90;
            Q90=makeQuery(id+"F0.imprint","IMPRINT",FACE,{"disambiguationData":[TD([[makeQuery(id+"F0.imprint","IMPRINT",EDGE,{"derivedFrom":sQuery(id+"F0.wireOp",EDGE,"E3.0.8.11")}),1.0]])]});
            var Q91;
            Q91=makeQuery(id+"F0.imprint","IMPRINT",FACE,{"disambiguationData":[TD([[makeQuery(id+"F0.imprint","IMPRINT",EDGE,{"derivedFrom":sQuery(id+"F0.wireOp",EDGE,"E3.0.7.10")}),1.0]])]});
            var Q92;
            Q92=makeQuery(id+"F0.imprint","IMPRINT",FACE,{"disambiguationData":[TD([[makeQuery(id+"F0.imprint","IMPRINT",EDGE,{"derivedFrom":sQuery(id+"F0.wireOp",EDGE,"E3.0.6.9")}),1.0]])]});
            var Q93;
            Q93=makeQuery(id+"F0.imprint","IMPRINT",FACE,{"disambiguationData":[TD([[makeQuery(id+"F0.imprint","IMPRINT",EDGE,{"derivedFrom":sQuery(id+"F0.wireOp",EDGE,"E2.0.0.11")}),1.0]])]});
            var Q94;
            Q94=makeQuery(id+"F0.imprint","IMPRINT",FACE,{"disambiguationData":[TD([[makeQuery(id+"F0.imprint","IMPRINT",EDGE,{"derivedFrom":sQuery(id+"F0.wireOp",EDGE,"E3.0.5.9")}),1.0]])]});
            var Q95;
            Q95=makeQuery(id+"F0.imprint","IMPRINT",FACE,{"disambiguationData":[TD([[makeQuery(id+"F0.imprint","IMPRINT",EDGE,{"derivedFrom":sQuery(id+"F0.wireOp",EDGE,"E3.0.4.8")}),1.0]])]});
            var Q96;
            Q96=makeQuery(id+"F0.imprint","IMPRINT",FACE,{"disambiguationData":[TD([[makeQuery(id+"F0.imprint","IMPRINT",EDGE,{"derivedFrom":sQuery(id+"F0.wireOp",EDGE,"E2.0.3.7")}),1.0]])]});
            var Q97;
            Q97=makeQuery(id+"F0.imprint","IMPRINT",FACE,{"disambiguationData":[TD([[makeQuery(id+"F0.imprint","IMPRINT",EDGE,{"derivedFrom":sQuery(id+"F0.wireOp",EDGE,"E2.0.2.3")}),1.0]])]});
            var Q98;
            Q98=makeQuery(id+"F0.imprint","IMPRINT",FACE,{"disambiguationData":[TD([[makeQuery(id+"F0.imprint","IMPRINT",EDGE,{"derivedFrom":sQuery(id+"F0.wireOp",EDGE,"E3.0.9.13")}),1.0]])]});
            var Q99;
            Q99=makeQuery(id+"F0.imprint","IMPRINT",FACE,{"disambiguationData":[TD([[makeQuery(id+"F0.imprint","IMPRINT",EDGE,{"derivedFrom":sQuery(id+"F0.wireOp",EDGE,"E3.0.8.12")}),1.0]])]});
            var Q100;
            Q100=makeQuery(id+"F0.imprint","IMPRINT",FACE,{"disambiguationData":[TD([[makeQuery(id+"F0.imprint","IMPRINT",EDGE,{"derivedFrom":sQuery(id+"F0.wireOp",EDGE,"E3.0.7.11")}),1.0]])]});
            var Q101;
            Q101=makeQuery(id+"F0.imprint","IMPRINT",FACE,{"disambiguationData":[TD([[makeQuery(id+"F0.imprint","IMPRINT",EDGE,{"derivedFrom":sQuery(id+"F0.wireOp",EDGE,"E3.0.6.10")}),1.0]])]});
            var Q102;
            Q102=makeQuery(id+"F0.imprint","IMPRINT",FACE,{"disambiguationData":[TD([[makeQuery(id+"F0.imprint","IMPRINT",EDGE,{"derivedFrom":sQuery(id+"F0.wireOp",EDGE,"E2.0.0.12")}),1.0]])]});
            var Q103;
            Q103=makeQuery(id+"F0.imprint","IMPRINT",FACE,{"disambiguationData":[TD([[makeQuery(id+"F0.imprint","IMPRINT",EDGE,{"derivedFrom":sQuery(id+"F0.wireOp",EDGE,"E3.0.5.10")}),1.0]])]});
            var Q104;
            Q104=makeQuery(id+"F0.imprint","IMPRINT",FACE,{"disambiguationData":[TD([[makeQuery(id+"F0.imprint","IMPRINT",EDGE,{"derivedFrom":sQuery(id+"F0.wireOp",EDGE,"E3.0.4.9")}),1.0]])]});
            var Q105;
            Q105=makeQuery(id+"F0.imprint","IMPRINT",FACE,{"disambiguationData":[TD([[makeQuery(id+"F0.imprint","IMPRINT",EDGE,{"derivedFrom":sQuery(id+"F0.wireOp",EDGE,"E2.0.3.8")}),1.0]])]});
            var Q106;
            Q106=makeQuery(id+"F0.imprint","IMPRINT",FACE,{"disambiguationData":[TD([[makeQuery(id+"F0.imprint","IMPRINT",EDGE,{"derivedFrom":sQuery(id+"F0.wireOp",EDGE,"E2.0.2.4")}),1.0]])]});
            var Q107;
            Q107=makeQuery(id+"F0.imprint","IMPRINT",FACE,{"disambiguationData":[TD([[makeQuery(id+"F0.imprint","IMPRINT",EDGE,{"derivedFrom":sQuery(id+"F0.wireOp",EDGE,"E3.0.9.14")}),1.0]])]});
            var Q108;
            Q108=makeQuery(id+"F0.imprint","IMPRINT",FACE,{"disambiguationData":[TD([[makeQuery(id+"F0.imprint","IMPRINT",EDGE,{"derivedFrom":sQuery(id+"F0.wireOp",EDGE,"E3.0.8.13")}),1.0]])]});
            var Q109;
            Q109=makeQuery(id+"F0.imprint","IMPRINT",FACE,{"disambiguationData":[TD([[makeQuery(id+"F0.imprint","IMPRINT",EDGE,{"derivedFrom":sQuery(id+"F0.wireOp",EDGE,"E3.0.7.12")}),1.0]])]});
            var Q110;
            Q110=makeQuery(id+"F0.imprint","IMPRINT",FACE,{"disambiguationData":[TD([[makeQuery(id+"F0.imprint","IMPRINT",EDGE,{"derivedFrom":sQuery(id+"F0.wireOp",EDGE,"E3.0.6.11")}),1.0]])]});
            var Q111;
            Q111=makeQuery(id+"F0.imprint","IMPRINT",FACE,{"disambiguationData":[TD([[makeQuery(id+"F0.imprint","IMPRINT",EDGE,{"derivedFrom":sQuery(id+"F0.wireOp",EDGE,"E3.0.7.13")}),1.0]])]});
            var Q112;
            Q112=makeQuery(id+"F0.imprint","IMPRINT",FACE,{"disambiguationData":[TD([[makeQuery(id+"F0.imprint","IMPRINT",EDGE,{"derivedFrom":sQuery(id+"F0.wireOp",EDGE,"E3.0.6.12")}),1.0]])]});
            var Q113;
            Q113=makeQuery(id+"F0.imprint","IMPRINT",FACE,{"disambiguationData":[TD([[makeQuery(id+"F0.imprint","IMPRINT",EDGE,{"derivedFrom":sQuery(id+"F0.wireOp",EDGE,"E3.0.5.11")}),1.0]])]});
            var Q114;
            Q114=makeQuery(id+"F0.imprint","IMPRINT",FACE,{"disambiguationData":[TD([[makeQuery(id+"F0.imprint","IMPRINT",EDGE,{"derivedFrom":sQuery(id+"F0.wireOp",EDGE,"E3.0.4.10")}),1.0]])]});
            var Q115;
            Q115=makeQuery(id+"F0.imprint","IMPRINT",FACE,{"disambiguationData":[TD([[makeQuery(id+"F0.imprint","IMPRINT",EDGE,{"derivedFrom":sQuery(id+"F0.wireOp",EDGE,"E3.0.8.14")}),1.0]])]});
            var Q116;
            Q116=makeQuery(id+"F0.imprint","IMPRINT",FACE,{"disambiguationData":[TD([[makeQuery(id+"F0.imprint","IMPRINT",EDGE,{"derivedFrom":sQuery(id+"F0.wireOp",EDGE,"E2.0.3.9")}),1.0]])]});
            var Q117;
            Q117=makeQuery(id+"F0.imprint","IMPRINT",FACE,{"disambiguationData":[TD([[makeQuery(id+"F0.imprint","IMPRINT",EDGE,{"derivedFrom":sQuery(id+"F0.wireOp",EDGE,"E2.0.2.5")}),1.0]])]});
            var Q118;
            Q118=makeQuery(id+"F0.imprint","IMPRINT",FACE,{"disambiguationData":[TD([[makeQuery(id+"F0.imprint","IMPRINT",EDGE,{"derivedFrom":sQuery(id+"F0.wireOp",EDGE,"E2.0.0.13")}),1.0]])]});
            var Q119;
            Q119=makeQuery(id+"F0.imprint","IMPRINT",FACE,{"disambiguationData":[TD([[makeQuery(id+"F0.imprint","IMPRINT",EDGE,{"derivedFrom":sQuery(id+"F0.wireOp",EDGE,"E2.0.0.6")}),1.0]])]});
            var Q120;
            Q120=makeQuery(id+"F0.imprint","IMPRINT",FACE,{"disambiguationData":[TD([[makeQuery(id+"F0.imprint","IMPRINT",EDGE,{"derivedFrom":sQuery(id+"F0.wireOp",EDGE,"E2.0.0.4")}),1.0]])]});
            var Q121;
            Q121=makeQuery(id+"F0.imprint","IMPRINT",FACE,{"disambiguationData":[TD([[makeQuery(id+"F0.imprint","IMPRINT",EDGE,{"derivedFrom":sQuery(id+"F0.wireOp",EDGE,"E2.0.0.5")}),1.0]])]});
            var Q122;
            Q122=makeQuery(id+"F0.imprint","IMPRINT",FACE,{"disambiguationData":[TD([[makeQuery(id+"F0.imprint","IMPRINT",EDGE,{"derivedFrom":sQuery(id+"F0.wireOp",EDGE,"E3.0.9.0")}),1.0]])]});
            var Q123;
            Q123=makeQuery(id+"F0.imprint","IMPRINT",FACE,{"disambiguationData":[TD([[makeQuery(id+"F0.imprint","IMPRINT",EDGE,{"derivedFrom":sQuery(id+"F0.wireOp",EDGE,"E2.0.0.3")}),1.0]])]});
            var Q124;
            Q124=makeQuery(id+"F0.imprint","IMPRINT",FACE,{"disambiguationData":[TD([[makeQuery(id+"F0.imprint","IMPRINT",EDGE,{"derivedFrom":sQuery(id+"F0.wireOp",EDGE,"E2.0.3.10")}),1.0]])]});
            var Q125;
            Q125=makeQuery(id+"F0.imprint","IMPRINT",FACE,{"disambiguationData":[TD([[makeQuery(id+"F0.imprint","IMPRINT",EDGE,{"derivedFrom":sQuery(id+"F0.wireOp",EDGE,"E2.0.2.6")}),1.0]])]});
            var Q126;
            Q126=makeQuery(id+"F0.imprint","IMPRINT",FACE,{"disambiguationData":[TD([[makeQuery(id+"F0.imprint","IMPRINT",EDGE,{"derivedFrom":sQuery(id+"F0.wireOp",EDGE,"E2.0.0.14")}),1.0]])]});
            var Q127;
            Q127=makeQuery(id+"F0.imprint","IMPRINT",FACE,{"disambiguationData":[TD([[makeQuery(id+"F0.imprint","IMPRINT",EDGE,{"derivedFrom":sQuery(id+"F0.wireOp",EDGE,"E3.0.7.14")}),1.0]])]});
            var Q128;
            Q128=makeQuery(id+"F0.imprint","IMPRINT",FACE,{"disambiguationData":[TD([[makeQuery(id+"F0.imprint","IMPRINT",EDGE,{"derivedFrom":sQuery(id+"F0.wireOp",EDGE,"E3.0.6.13")}),1.0]])]});
            var Q129;
            Q129=makeQuery(id+"F0.imprint","IMPRINT",FACE,{"disambiguationData":[TD([[makeQuery(id+"F0.imprint","IMPRINT",EDGE,{"derivedFrom":sQuery(id+"F0.wireOp",EDGE,"E3.0.5.12")}),1.0]])]});
            var Q130;
            Q130=makeQuery(id+"F0.imprint","IMPRINT",FACE,{"disambiguationData":[TD([[makeQuery(id+"F0.imprint","IMPRINT",EDGE,{"derivedFrom":sQuery(id+"F0.wireOp",EDGE,"E3.0.4.11")}),1.0]])]});
            var Q131;
            Q131=makeQuery(id+"F0.imprint","IMPRINT",FACE,{"disambiguationData":[TD([[makeQuery(id+"F0.imprint","IMPRINT",EDGE,{"derivedFrom":sQuery(id+"F0.wireOp",EDGE,"E2.0.3.11")}),1.0]])]});
            var Q132;
            Q132=makeQuery(id+"F0.imprint","IMPRINT",FACE,{"disambiguationData":[TD([[makeQuery(id+"F0.imprint","IMPRINT",EDGE,{"derivedFrom":sQuery(id+"F0.wireOp",EDGE,"E2.0.2.7")}),1.0]])]});
            var Q133;
            Q133=makeQuery(id+"F0.imprint","IMPRINT",FACE,{"disambiguationData":[TD([[makeQuery(id+"F0.imprint","IMPRINT",EDGE,{"derivedFrom":sQuery(id+"F0.wireOp",EDGE,"E2.0.1.3")}),1.0]])]});
            var Q134;
            Q134=makeQuery(id+"F0.imprint","IMPRINT",FACE,{"disambiguationData":[TD([[makeQuery(id+"F0.imprint","IMPRINT",EDGE,{"derivedFrom":sQuery(id+"F0.wireOp",EDGE,"E3.0.8.0")}),1.0]])]});
            var Q135;
            Q135=makeQuery(id+"F0.imprint","IMPRINT",FACE,{"disambiguationData":[TD([[makeQuery(id+"F0.imprint","IMPRINT",EDGE,{"derivedFrom":sQuery(id+"F0.wireOp",EDGE,"E3.0.6.14")}),1.0]])]});
            var Q136;
            Q136=makeQuery(id+"F0.imprint","IMPRINT",FACE,{"disambiguationData":[TD([[makeQuery(id+"F0.imprint","IMPRINT",EDGE,{"derivedFrom":sQuery(id+"F0.wireOp",EDGE,"E3.0.8.10")}),1.0]])]});
            var Q137;
            Q137=makeQuery(id+"F0.imprint","IMPRINT",FACE,{"disambiguationData":[TD([[makeQuery(id+"F0.imprint","IMPRINT",EDGE,{"derivedFrom":sQuery(id+"F0.wireOp",EDGE,"E3.0.9.1")}),1.0]])]});
            var Q138;
            Q138=makeQuery(id+"F0.imprint","IMPRINT",FACE,{"disambiguationData":[TD([[makeQuery(id+"F0.imprint","IMPRINT",EDGE,{"derivedFrom":sQuery(id+"F0.wireOp",EDGE,"E2.0.0.9")}),1.0]])]});
            var Q139;
            Q139=makeQuery(id+"F0.imprint","IMPRINT",FACE,{"disambiguationData":[TD([[makeQuery(id+"F0.imprint","IMPRINT",EDGE,{"derivedFrom":sQuery(id+"F0.wireOp",EDGE,"E2.0.2.14")}),1.0]])]});
            var Q140;
            Q140=makeQuery(id+"F0.imprint","IMPRINT",FACE,{"disambiguationData":[TD([[makeQuery(id+"F0.imprint","IMPRINT",EDGE,{"derivedFrom":sQuery(id+"F0.wireOp",EDGE,"E3.0.5.13")}),1.0]])]});
            var Q141;
            Q141=makeQuery(id+"F0.imprint","IMPRINT",FACE,{"disambiguationData":[TD([[makeQuery(id+"F0.imprint","IMPRINT",EDGE,{"derivedFrom":sQuery(id+"F0.wireOp",EDGE,"E3.0.8.1")}),1.0]])]});
            var Q142;
            Q142=makeQuery(id+"F0.imprint","IMPRINT",FACE,{"disambiguationData":[TD([[makeQuery(id+"F0.imprint","IMPRINT",EDGE,{"derivedFrom":sQuery(id+"F0.wireOp",EDGE,"E2.0.1.10")}),1.0]])]});
            var Q143;
            Q143=makeQuery(id+"F0.imprint","IMPRINT",FACE,{"disambiguationData":[TD([[makeQuery(id+"F0.imprint","IMPRINT",EDGE,{"derivedFrom":sQuery(id+"F0.wireOp",EDGE,"E2.0.3.12")}),1.0]])]});
            var Q144;
            Q144=makeQuery(id+"F0.imprint","IMPRINT",FACE,{"disambiguationData":[TD([[makeQuery(id+"F0.imprint","IMPRINT",EDGE,{"derivedFrom":sQuery(id+"F0.wireOp",EDGE,"E2.0.2.8")}),1.0]])]});
            var Q145;
            Q145=makeQuery(id+"F0.imprint","IMPRINT",FACE,{"disambiguationData":[TD([[makeQuery(id+"F0.imprint","IMPRINT",EDGE,{"derivedFrom":sQuery(id+"F0.wireOp",EDGE,"E2.0.1.4")}),1.0]])]});
            var Q146;
            Q146=makeQuery(id+"F0.imprint","IMPRINT",FACE,{"disambiguationData":[TD([[makeQuery(id+"F0.imprint","IMPRINT",EDGE,{"derivedFrom":sQuery(id+"F0.wireOp",EDGE,"E3.0.4.13")}),1.0]])]});
            var Q147;
            Q147=makeQuery(id+"F0.imprint","IMPRINT",FACE,{"disambiguationData":[TD([[makeQuery(id+"F0.imprint","IMPRINT",EDGE,{"derivedFrom":sQuery(id+"F0.wireOp",EDGE,"E3.0.9.8")}),1.0]])]});
            var Q148;
            Q148=makeQuery(id+"F0.imprint","IMPRINT",FACE,{"disambiguationData":[TD([[makeQuery(id+"F0.imprint","IMPRINT",EDGE,{"derivedFrom":sQuery(id+"F0.wireOp",EDGE,"E3.0.8.7")}),1.0]])]});
            var Q149;
            Q149=makeQuery(id+"F0.imprint","IMPRINT",FACE,{"disambiguationData":[TD([[makeQuery(id+"F0.imprint","IMPRINT",EDGE,{"derivedFrom":sQuery(id+"F0.wireOp",EDGE,"E3.0.9.2")}),1.0]])]});
            extrude(context, id + "F1", {"entities" : qUnion([Q0, Q1, Q2, Q3, Q4, Q5, Q6, Q7, Q8, Q9, Q10, Q11, Q12, Q13, Q14, Q15, Q16, Q17, Q18, Q19, Q20, Q21, Q22, Q23, Q24, Q25, Q26, Q27, Q28, Q29, Q30, Q31, Q32, Q33, Q34, Q35, Q36, Q37, Q38, Q39, Q40, Q41, Q42, Q43, Q44, Q45, Q46, Q47, Q48, Q49, Q50, Q51, Q52, Q53, Q54, Q55, Q56, Q57, Q58, Q59, Q60, Q61, Q62, Q63, Q64, Q65, Q66, Q67, Q68, Q69, Q70, Q71, Q72, Q73, Q74, Q75, Q76, Q77, Q78, Q79, Q80, Q81, Q82, Q83, Q84, Q85, Q86, Q87, Q88, Q89, Q90, Q91, Q92, Q93, Q94, Q95, Q96, Q97, Q98, Q99, Q100, Q101, Q102, Q103, Q104, Q105, Q106, Q107, Q108, Q109, Q110, Q111, Q112, Q113, Q114, Q115, Q116, Q117, Q118, Q119, Q120, Q121, Q122, Q123, Q124, Q125, Q126, Q127, Q128, Q129, Q130, Q131, Q132, Q133, Q134, Q135, Q136, Q137, Q138, Q139, Q140, Q141, Q142, Q143, Q144, Q145, Q146, Q147, Q148, Q149]), "depth" : 0.5 * mm});
        }
    });
